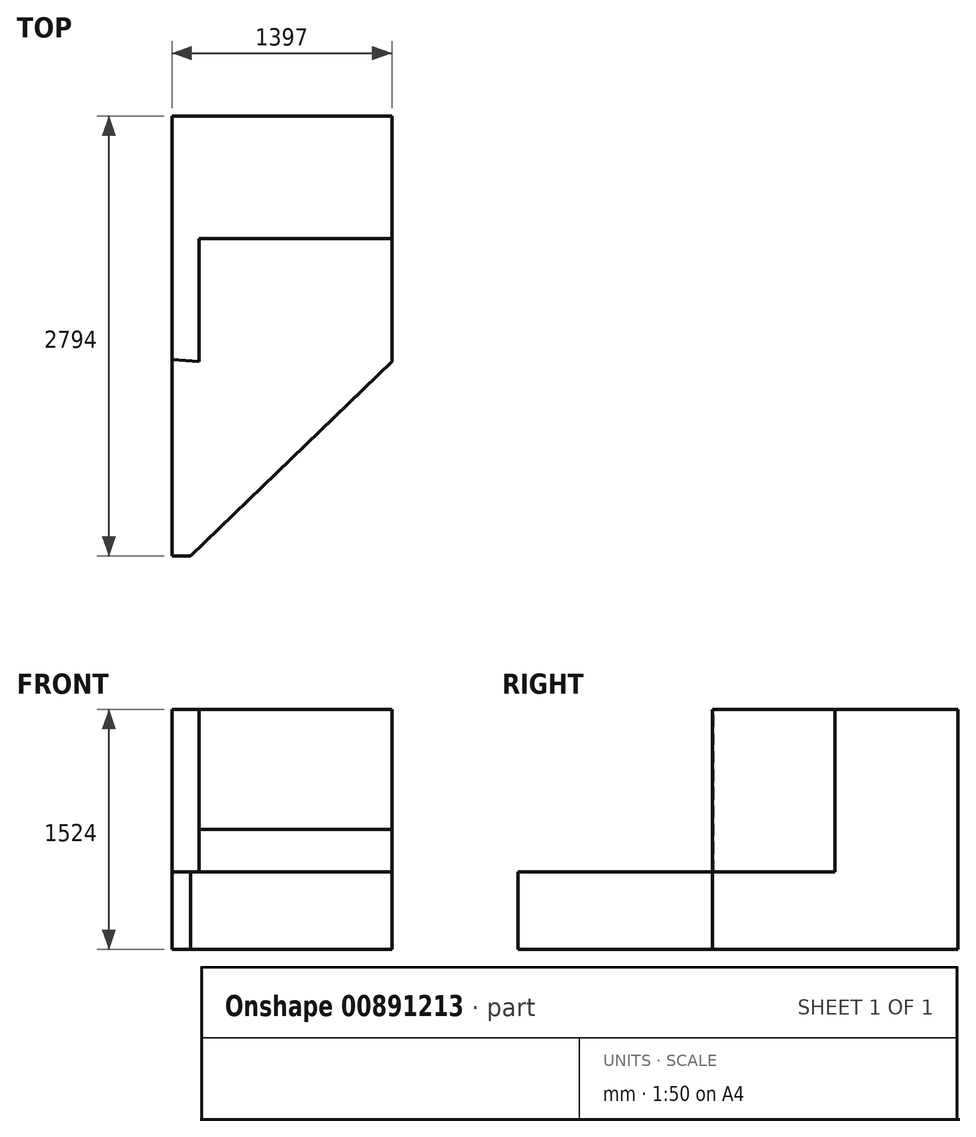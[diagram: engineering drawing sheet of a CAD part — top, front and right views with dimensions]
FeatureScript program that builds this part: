
annotation { "Feature Type Name" : "Feature", "Feature Type Description" : "" }
export const myFeature = defineFeature(function(context is Context, id is Id, definition is map)
    precondition{}
    {
        {
            var Q0;
            Q0=qCreatedBy(makeId("Front.planeOp"),FACE);
            var sketch = newSketch(context, id + "F0", { "sketchPlane" : qUnion([Q0])});
            skLineSegment(sketch, "E0.bottom", {"start": v(1278.78, 0) * mm, "end": v(-118.22, 0) * mm});
            skLineSegment(sketch, "E0.top", {"start": v(1278.78, 1524) * mm, "end": v(-118.22, 1524) * mm});
            skLineSegment(sketch, "E0.left", {"start": v(1278.78, 0) * mm, "end": v(1278.78, 1524) * mm});
            skLineSegment(sketch, "E0.right", {"start": v(-118.22, 0) * mm, "end": v(-118.22, 1524) * mm});
            skSolve(sketch);
        }
        {
            var Q0;
            Q0=makeQuery(id+"F0.imprint","IMPRINT",FACE,{"disambiguationData":[TD([[makeQuery(id+"F0.imprint","IMPRINT",EDGE,{"derivedFrom":sQuery(id+"F0.wireOp",EDGE,"E0.bottom")}),-1.0]])]});
            var sketch = newSketch(context, id + "F1", { "sketchPlane" : qUnion([Q0])});
            skSolve(sketch);
        }
        {
            var Q0;
            Q0 = qSketchRegion(id + "F1", true);
            var Q1;
            Q1=makeQuery(id+"F0.imprint","IMPRINT",FACE,{"disambiguationData":[TD([[makeQuery(id+"F0.imprint","IMPRINT",EDGE,{"derivedFrom":sQuery(id+"F0.wireOp",EDGE,"E0.bottom")}),-1.0]])]});
            extrude(context, id + "F2", {"entities" : qUnion([Q0, Q1]), "depth" : 2794 * mm, "offsetDistance" : 25.4 * mm});
        }
        {
            var Q0;
            Q0=makeQuery(id+"F2.opExtrude","SWEPT_FACE",FACE,{"disambiguationData":[OSD([sQuery(id+"F0.wireOp",EDGE,"E0.top")])]});
            var sketch = newSketch(context, id + "F3", { "sketchPlane" : qUnion([Q0])});
            skLineSegment(sketch, "E1", {"start": v(0, -2794) * mm, "end": v(1278.78, -1558.69) * mm});
            skSolve(sketch);
        }
        {
            var Q0;
            {var subQ0=sQuery(id+"F3.wireOp",EDGE,"E1");Q0=makeQuery(id+"F3.imprint","IMPRINT",FACE,{"disambiguationData":[TD([[makeQuery(id+"F3.imprint","IMPRINT",EDGE,{"derivedFrom":subQ0}),-1.0]])]});}
            var sketch = newSketch(context, id + "F4", { "sketchPlane" : qUnion([Q0])});
            skSolve(sketch);
        }
        {
            var Q0;
            Q0 = qSketchRegion(id + "F4", true);
            var Q1;
            {var subQ0=sQuery(id+"F3.wireOp",EDGE,"E1");Q1=makeQuery(id+"F3.imprint","IMPRINT",FACE,{"disambiguationData":[TD([[makeQuery(id+"F3.imprint","IMPRINT",EDGE,{"derivedFrom":subQ0}),-1.0]])]});}
            extrude(context, id + "F5", {"entities" : qUnion([Q0, Q1]), "operationType" : NewBodyOperationType.REMOVE, "oppositeDirection" : true, "depth" : 2021.84 * mm, "offsetDistance" : 25.4 * mm});
        }
        {
            var Q0;
            Q0=makeQuery(id+"F2.opExtrude","SWEPT_FACE",FACE,{"disambiguationData":[OSD([sQuery(id+"F0.wireOp",EDGE,"E0.left")])]});
            var sketch = newSketch(context, id + "F6", { "sketchPlane" : qUnion([Q0])});
            skLineSegment(sketch, "E2.bottom", {"start": v(-779.34, 1524) * mm, "end": v(-1795.34, 1524) * mm});
            skLineSegment(sketch, "E2.top", {"start": v(-779.34, 762) * mm, "end": v(-1795.34, 762) * mm});
            skLineSegment(sketch, "E2.left", {"start": v(-779.34, 1524) * mm, "end": v(-779.34, 762) * mm});
            skLineSegment(sketch, "E2.right", {"start": v(-1795.34, 1524) * mm, "end": v(-1795.34, 762) * mm});
            skSolve(sketch);
        }
        {
            var Q0;
            {var subQ5=sQuery(id+"F6.wireOp",EDGE,"E2.left");Q0=makeQuery(id+"F6.imprint","IMPRINT",FACE,{"disambiguationData":[TD([[makeQuery(id+"F6.imprint","IMPRINT",EDGE,{"derivedFrom":subQ5}),-1.0]])]});}
            extrude(context, id + "F7", {"entities" : qUnion([Q0]), "operationType" : NewBodyOperationType.REMOVE, "oppositeDirection" : true, "depth" : 1224.28 * mm, "offsetDistance" : 25.4 * mm});
        }
        {
            var Q0;
            Q0=makeQuery(id+"F2.opExtrude","CAP_FACE",FACE,{"disambiguationData":[OSD([sQuery(id+"F0.wireOp",EDGE,"E0.bottom"),sQuery(id+"F0.wireOp",EDGE,"E0.top"),sQuery(id+"F0.wireOp",EDGE,"E0.left"),sQuery(id+"F0.wireOp",EDGE,"E0.right")])],"isStart":false});
            var sketch = newSketch(context, id + "F8", { "sketchPlane" : qUnion([Q0])});
            skLineSegment(sketch, "E3", {"start": v(-118.22, 490.77) * mm, "end": v(0, 490.77) * mm});
            skLineSegment(sketch, "E4", {"start": v(0, 490.77) * mm, "end": v(2508.24, 1992.15) * mm});
            skSolve(sketch);
        }
        {
            var Q0;
            Q0=makeQuery(id+"F2.opExtrude","SWEPT_FACE",FACE,{"disambiguationData":[OSD([sQuery(id+"F0.wireOp",EDGE,"E0.top")])]});
            var sketch = newSketch(context, id + "F9", { "sketchPlane" : qUnion([Q0])});
            skLineSegment(sketch, "E5", {"start": v(54.5, -1558.69) * mm, "end": v(-118.22, -1547.75) * mm});
            skSolve(sketch);
        }
        {
            var Q0;
            {var subQ3=sQuery(id+"F9.wireOp",EDGE,"E5");Q0=makeQuery(id+"F9.imprint","IMPRINT",FACE,{"disambiguationData":[TD([[makeQuery(id+"F9.imprint","IMPRINT",EDGE,{"derivedFrom":subQ3}),1.0]])]});}
            var sketch = newSketch(context, id + "F10", { "sketchPlane" : qUnion([Q0])});
            skSolve(sketch);
        }
        {
            var Q0;
            Q0 = qSketchRegion(id + "F10", true);
            var Q1;
            {var subQ3=sQuery(id+"F9.wireOp",EDGE,"E5");Q1=makeQuery(id+"F10.imprint","IMPRINT",FACE,{"disambiguationData":[TD([[makeQuery(id+"F10.imprint","IMPRINT",EDGE,{"derivedFrom":makeQuery(id+"F9.imprint","IMPRINT",EDGE,{"derivedFrom":subQ3})}),1.0]])]});}
            extrude(context, id + "F11", {"entities" : qUnion([Q0, Q1]), "operationType" : NewBodyOperationType.REMOVE, "oppositeDirection" : true, "depth" : 1031.24 * mm, "offsetDistance" : 25.4 * mm});
        }
        {
            var Q0;
            Q0=makeQuery(id+"F11.boolean.opBoolean","COPY",FACE,{"derivedFrom":makeQuery(id+"F11.opExtrude","SWEPT_FACE",FACE,{"disambiguationData":[OSD([sQuery(id+"F0.wireOp",EDGE,"E0.top"),sQuery(id+"F0.wireOp",EDGE,"E0.left"),sQuery(id+"F3.wireOp",EDGE,"E1"),sQuery(id+"F6.wireOp",EDGE,"E2.bottom")])]})});
            var sketch = newSketch(context, id + "F12", { "sketchPlane" : qUnion([Q0])});
            skSolve(sketch);
        }
        {
            var Q0;
            {var subQ0=sQuery(id+"F6.wireOp",EDGE,"E2.bottom");var subQ1=sQuery(id+"F3.wireOp",EDGE,"E1");var subQ2=sQuery(id+"F0.wireOp",EDGE,"E0.left");var subQ3=sQuery(id+"F0.wireOp",EDGE,"E0.top");Q0=makeQuery(id+"F12.imprint","IMPRINT",FACE,{"disambiguationData":[TD([[makeQuery(id+"F12.imprint","IMPRINT",EDGE,{"derivedFrom":makeQuery(id+"F11.boolean.opBoolean","COPY",EDGE,{"derivedFrom":makeQuery(id+"F11.opExtrude","CAP_EDGE",EDGE,{"disambiguationData":[OSD([subQ3,subQ2,subQ1,subQ0])],"isStart":false})})}),1.0]])]});}
            extrude(context, id + "F13", {"entities" : qUnion([Q0]), "operationType" : NewBodyOperationType.REMOVE, "oppositeDirection" : true, "depth" : 779.78 * mm, "offsetDistance" : 25.4 * mm});
        }
    });
